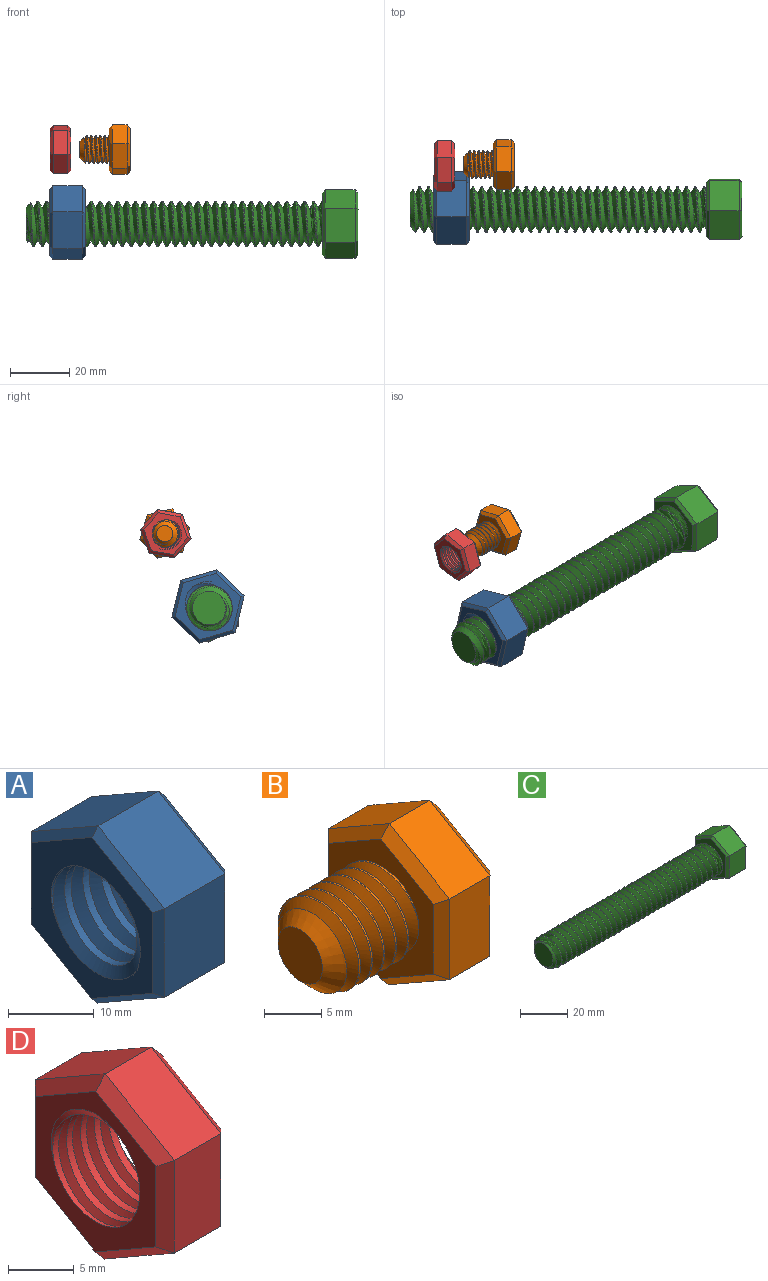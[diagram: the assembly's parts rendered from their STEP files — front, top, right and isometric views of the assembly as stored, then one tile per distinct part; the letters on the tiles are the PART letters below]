
ASSEMBLY  parts=4 mates=2
PART A: 23 faces, bbox 15.4x22.9x26.3 mm
  f0: cylinder r=6.7mm len=13.39mm, axis (1,0,0), area 180.9mm2, adj f7,f8,f21,f22
  f1: plane 10.98x10mm, normal (0,-0.5,0.86), area 127mm2, adj f2,f6,f14,f18
  f2: plane 12.7x10mm, normal (0,-1,0), area 127mm2, adj f1,f3,f12,f16
  f3: plane 11.02x10mm, normal (0,-0.5,-0.87), area 127mm2, adj f2,f4,f10,f15
  f4: plane 10.98x10mm, normal (0,0.5,-0.86), area 127mm2, adj f3,f5,f9,f17
  f5: plane 12.7x10mm, normal (0,1,0), area 127mm2, adj f4,f6,f11,f19
  f6: plane 11.02x10mm, normal (0,0.5,0.87), area 127mm2, adj f1,f5,f13,f20
  f7: plane 24.01x20.94mm, normal (-1,0,0), area 180.5mm2, adj f0,f9,f10,f11,f12,f13,f14,f21
  f8: plane 24.01x20.94mm, normal (1,0,0), area 180.5mm2, adj f0,f15,f16,f17,f18,f19,f20,f21
  f9: plane 10.99x6.96mm, normal (-0.71,0.36,-0.61), area 17.1mm2, adj f4,f7,f10,f11
  f10: plane 11.02x6.9mm, normal (-0.71,-0.35,-0.61), area 17.1mm2, adj f3,f7,f9,f12
  f11: plane 12.7x1.03mm, normal (-0.71,0.71,0), area 17.1mm2, adj f5,f7,f9,f13
  f12: plane 12.7x1.03mm, normal (-0.71,-0.71,0), area 17.1mm2, adj f2,f7,f10,f14
  f13: plane 11.02x6.9mm, normal (-0.71,0.35,0.61), area 17.1mm2, adj f6,f7,f11,f14
  f14: plane 10.99x6.96mm, normal (-0.71,-0.36,0.61), area 17.1mm2, adj f1,f7,f12,f13
  f15: plane 11.02x6.9mm, normal (0.71,-0.35,-0.61), area 17.1mm2, adj f3,f8,f16,f17
  f16: plane 12.7x1.03mm, normal (0.71,-0.71,0), area 17.1mm2, adj f2,f8,f15,f18
  f17: plane 10.99x6.96mm, normal (0.71,0.36,-0.61), area 17.1mm2, adj f4,f8,f15,f19
  f18: plane 10.99x6.96mm, normal (0.71,-0.36,0.61), area 17.1mm2, adj f1,f8,f16,f20
  f19: plane 12.7x1.03mm, normal (0.71,0.71,0), area 17.1mm2, adj f5,f8,f17,f20
  f20: plane 11.02x6.9mm, normal (0.71,0.35,0.61), area 17.1mm2, adj f6,f8,f18,f19
  f21: bspline ~19.36x16.77mm, area 370.1mm2, adj f0,f7,f8,f22
  f22: bspline ~19.36x16.77mm, area 370.1mm2, adj f0,f7,f8,f21
PART B: 25 faces, bbox 17.8x15.9x18.1 mm
  f0: cylinder r=4.75mm len=9.5mm, axis (1,0,0), area 28.1mm2, adj f1,f2,f4,f12
  f1: bspline ~10.97x9.91mm, area 196.7mm2, adj f0,f2,f4,f12
  f2: bspline ~10.97x10.66mm, area 196.6mm2, adj f0,f1,f4,f12
  f3: plane 5.5x5.5mm, normal (-1,0,0), area 23.8mm2, adj f4
  f4: cone r=4.75mm half-angle=45deg, axis (1,0,0), area 47.4mm2, adj f0,f1,f2,f3
  f5: plane 7.48x5mm, normal (0,-0.5,0.86), area 43.3mm2, adj f6,f10,f18,f22
  f6: plane 8.66x5mm, normal (0,-1,0), area 43.3mm2, adj f5,f7,f16,f20
  f7: plane 7.52x5mm, normal (0,-0.5,-0.87), area 43.3mm2, adj f6,f8,f14,f19
  f8: plane 7.48x5mm, normal (0,0.5,-0.86), area 43.3mm2, adj f7,f9,f13,f21
  f9: plane 8.66x5mm, normal (0,1,0), area 43.3mm2, adj f8,f10,f15,f23
  f10: plane 7.52x5mm, normal (0,0.5,0.87), area 43.3mm2, adj f5,f9,f17,f24
  f11: plane 15.01x13.03mm, normal (1,0,0), area 146.4mm2, adj f13,f14,f15,f16,f17,f18
  f12: plane 15.83x13.85mm, normal (-1,0,0), area 89.2mm2, adj f0,f1,f2,f19,f20,f21,f22,f23
  f13: plane 7.49x4.93mm, normal (0.71,0.36,-0.61), area 11.4mm2, adj f8,f11,f14,f15
  f14: plane 7.52x4.88mm, normal (0.71,-0.35,-0.61), area 11.4mm2, adj f7,f11,f13,f16
  f15: plane 8.66x1.03mm, normal (0.71,0.71,0), area 11.4mm2, adj f9,f11,f13,f17
  f16: plane 8.66x1.03mm, normal (0.71,-0.71,0), area 11.4mm2, adj f6,f11,f14,f18
  f17: plane 7.52x4.88mm, normal (0.71,0.35,0.61), area 11.4mm2, adj f10,f11,f15,f18
  f18: plane 7.49x4.93mm, normal (0.71,-0.36,0.61), area 11.4mm2, adj f5,f11,f16,f17
  f19: plane 7.52x4.88mm, normal (-0.71,-0.35,-0.61), area 11.4mm2, adj f7,f12,f20,f21
  f20: plane 8.66x1.03mm, normal (-0.71,-0.71,0), area 11.4mm2, adj f6,f12,f19,f22
  f21: plane 7.49x4.93mm, normal (-0.71,0.36,-0.61), area 11.4mm2, adj f8,f12,f19,f23
  f22: plane 7.49x4.93mm, normal (-0.71,-0.36,0.61), area 11.4mm2, adj f5,f12,f20,f24
  f23: plane 8.66x1.03mm, normal (-0.71,0.71,0), area 11.4mm2, adj f9,f12,f21,f24
  f24: plane 7.52x4.88mm, normal (-0.71,0.35,0.61), area 11.4mm2, adj f10,f12,f22,f23
PART C: 25 faces, bbox 113.4x20.1x23.2 mm
  f0: plane 10x9.98mm, normal (0,-0.5,0.86), area 115.5mm2, adj f1,f5,f18,f22
  f1: plane 11.55x10mm, normal (0,-1,0), area 115.5mm2, adj f0,f2,f16,f20
  f2: plane 10.02x10mm, normal (0,-0.5,-0.87), area 115.5mm2, adj f1,f3,f14,f19
  f3: plane 10x9.98mm, normal (0,0.5,-0.86), area 115.5mm2, adj f2,f4,f13,f21
  f4: plane 11.55x10mm, normal (0,1,0), area 115.5mm2, adj f3,f5,f15,f23
  f5: plane 10.02x10mm, normal (0,0.5,0.87), area 115.5mm2, adj f0,f4,f17,f24
  f6: plane 20.78x18.04mm, normal (1,0,0), area 280.6mm2, adj f13,f14,f15,f16,f17,f18
  f7: plane 20.78x18.04mm, normal (-1,0,0), area 138.6mm2, adj f8,f9,f10,f19,f20,f21,f22,f23
  f8: cylinder r=7.68mm len=98mm, axis (1,0,0), area 880mm2, adj f7,f9,f10,f12
  f9: bspline ~102.31x17.74mm, area 3572.1mm2, adj f7,f8,f10,f11,f12
  f10: bspline ~102.81x17.74mm, area 3583.5mm2, adj f7,f8,f9,f11,f12
  f11: plane 11.42x11.42mm, normal (-1,0,0), area 100.8mm2, adj f9,f10,f12
  f12: cone r=7.68mm half-angle=45deg, axis (1,0,0), area 58.2mm2, adj f8,f9,f10,f11
  f13: plane 9.98x6.38mm, normal (0.71,0.36,-0.61), area 15.5mm2, adj f3,f6,f14,f15
  f14: plane 10.02x6.32mm, normal (0.71,-0.35,-0.61), area 15.5mm2, adj f2,f6,f13,f16
  f15: plane 11.55x1.04mm, normal (0.71,0.71,0), area 15.5mm2, adj f4,f6,f13,f17
  f16: plane 11.55x1.04mm, normal (0.71,-0.71,0), area 15.5mm2, adj f1,f6,f14,f18
  f17: plane 10.02x6.32mm, normal (0.71,0.35,0.61), area 15.5mm2, adj f5,f6,f15,f18
  f18: plane 9.98x6.38mm, normal (0.71,-0.36,0.61), area 15.5mm2, adj f0,f6,f16,f17
  f19: plane 10.02x6.32mm, normal (-0.71,-0.35,-0.61), area 15.5mm2, adj f2,f7,f20,f21
  f20: plane 11.55x1.04mm, normal (-0.71,-0.71,0), area 15.5mm2, adj f1,f7,f19,f22
  f21: plane 9.98x6.38mm, normal (-0.71,0.36,-0.61), area 15.5mm2, adj f3,f7,f19,f23
  f22: plane 9.98x6.38mm, normal (-0.71,-0.36,0.61), area 15.5mm2, adj f0,f7,f20,f24
  f23: plane 11.55x1.04mm, normal (-0.71,0.71,0), area 15.5mm2, adj f4,f7,f21,f24
  f24: plane 10.02x6.32mm, normal (-0.71,0.35,0.61), area 15.5mm2, adj f5,f7,f22,f23
PART D: 23 faces, bbox 9.1x15.4x17.7 mm
  f0: plane 7.49x5mm, normal (0,-0.5,0.86), area 43.3mm2, adj f1,f5,f13,f17
  f1: plane 8.66x5mm, normal (0,-1,0), area 43.3mm2, adj f0,f2,f11,f15
  f2: plane 7.51x5mm, normal (0,-0.5,-0.87), area 43.3mm2, adj f1,f3,f9,f14
  f3: plane 7.49x5mm, normal (0,0.5,-0.86), area 43.3mm2, adj f2,f4,f8,f16
  f4: plane 8.66x5mm, normal (0,1,0), area 43.3mm2, adj f3,f5,f10,f18
  f5: plane 7.51x5mm, normal (0,0.5,0.87), area 43.3mm2, adj f0,f4,f12,f19
  f6: plane 15.37x13.38mm, normal (-1,0,0), area 71.4mm2, adj f8,f9,f10,f11,f12,f13,f20,f21
  f7: plane 15.37x13.38mm, normal (1,0,0), area 71.4mm2, adj f14,f15,f16,f17,f18,f19,f20,f21
  f8: plane 7.49x4.93mm, normal (-0.71,0.36,-0.61), area 11.4mm2, adj f3,f6,f9,f10
  f9: plane 7.51x4.89mm, normal (-0.71,-0.35,-0.61), area 11.4mm2, adj f2,f6,f8,f11
  f10: plane 8.66x1.02mm, normal (-0.71,0.71,0), area 11.4mm2, adj f4,f6,f8,f12
  f11: plane 8.66x1.02mm, normal (-0.71,-0.71,0), area 11.4mm2, adj f1,f6,f9,f13
  f12: plane 7.51x4.89mm, normal (-0.71,0.35,0.61), area 11.4mm2, adj f5,f6,f10,f13
  f13: plane 7.49x4.93mm, normal (-0.71,-0.36,0.61), area 11.4mm2, adj f0,f6,f11,f12
  f14: plane 7.51x4.89mm, normal (0.71,-0.35,-0.61), area 11.4mm2, adj f2,f7,f15,f16
  f15: plane 8.66x1.02mm, normal (0.71,-0.71,0), area 11.4mm2, adj f1,f7,f14,f17
  f16: plane 7.49x4.93mm, normal (0.71,0.36,-0.61), area 11.4mm2, adj f3,f7,f14,f18
  f17: plane 7.49x4.93mm, normal (0.71,-0.36,0.61), area 11.4mm2, adj f0,f7,f15,f19
  f18: plane 8.66x1.02mm, normal (0.71,0.71,0), area 11.4mm2, adj f4,f7,f16,f19
  f19: plane 7.51x4.89mm, normal (0.71,0.35,0.61), area 11.4mm2, adj f5,f7,f17,f18
  f20: cylinder r=4.66mm len=9.32mm, axis (1,0,0), area 85.4mm2, adj f6,f7,f21,f22
  f21: bspline ~12.5x10.82mm, area 128.4mm2, adj f6,f7,f20,f22
  f22: bspline ~12.5x10.82mm, area 128.5mm2, adj f6,f7,f20,f21
PLACE A rot(axis=(0,0.6,-0.8),180deg) t=(-55.27,-6.86,23.48)mm fixed
PLACE B rot(axis=(-1,0,0),43.8deg) t=(-31.66,7.73,48.08)mm
PLACE C rot(axis=(-1,0,0),178.1deg) t=(42.73,-7.35,22.96)mm
PLACE D rot(axis=(1,0,0),100.2deg) t=(-48.16,7.38,48.02)mm fixed
MATE cylindrical C.f8 <-> A.f7  axis (-1,0,0) through (-63.27,-7.35,22.96)mm
MATE cylindrical B.f0 <-> D.f6  axis (-1,0,0) through (-45.16,7.73,48.08)mm
